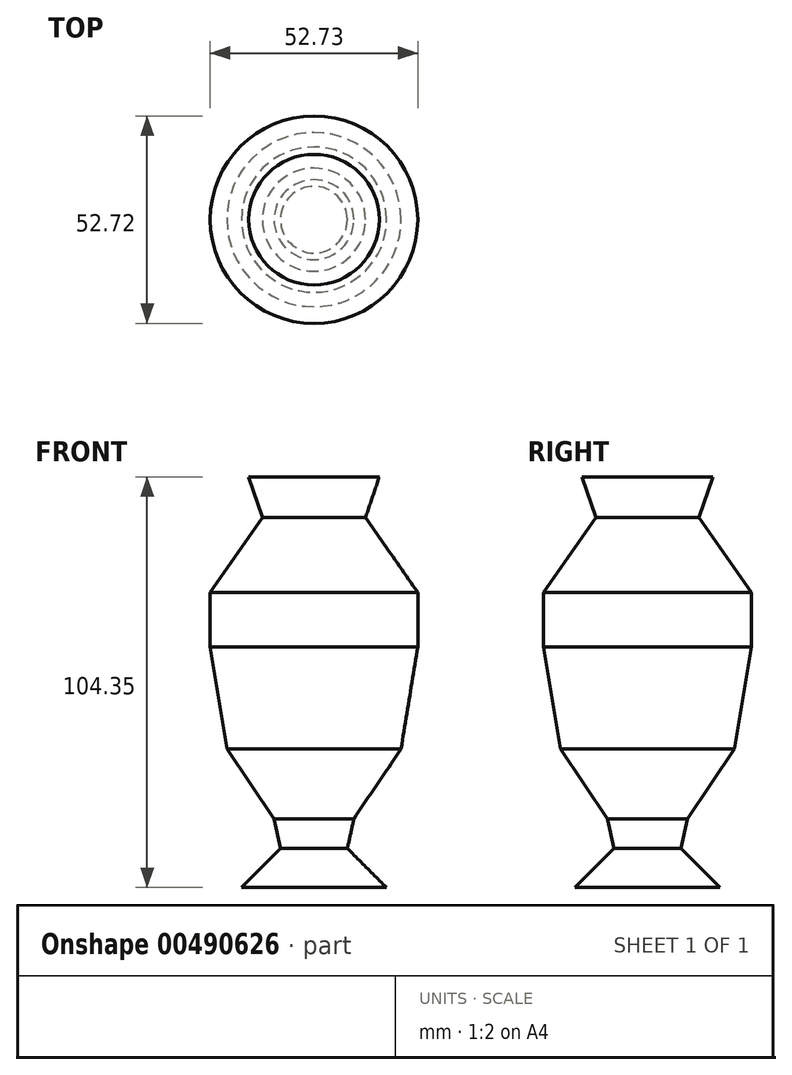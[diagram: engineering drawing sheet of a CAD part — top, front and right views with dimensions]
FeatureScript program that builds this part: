
annotation { "Feature Type Name" : "Feature", "Feature Type Description" : "" }
export const myFeature = defineFeature(function(context is Context, id is Id, definition is map)
    precondition{}
    {
        {
            var Q0;
            Q0=qCreatedBy(makeId("Front.planeOp"),FACE);
            var sketch = newSketch(context, id + "F0", { "sketchPlane" : qUnion([Q0])});
            skLineSegment(sketch, "E0", {"start": v(-34.1, 48.12) * mm, "end": v(-17.51, 48.12) * mm});
            skLineSegment(sketch, "E1", {"start": v(-17.51, 48.12) * mm, "end": v(-17.51, -56.23) * mm});
            skLineSegment(sketch, "E2", {"start": v(-17.51, -56.23) * mm, "end": v(-35.95, -56.23) * mm});
            skLineSegment(sketch, "E3", {"start": v(-35.95, -56.23) * mm, "end": v(-26, -46.27) * mm});
            skLineSegment(sketch, "E4", {"start": v(-26, -46.27) * mm, "end": v(-27.65, -38.71) * mm});
            skLineSegment(sketch, "E5", {"start": v(-27.65, -38.71) * mm, "end": v(-39.64, -21.02) * mm});
            skLineSegment(sketch, "E6", {"start": v(-39.64, -21.02) * mm, "end": v(-43.88, 4.98) * mm});
            skLineSegment(sketch, "E7", {"start": v(-43.88, 4.98) * mm, "end": v(-43.88, 18.8) * mm});
            skLineSegment(sketch, "E8", {"start": v(-43.88, 18.8) * mm, "end": v(-30.6, 37.8) * mm});
            skLineSegment(sketch, "E9", {"start": v(-30.6, 37.8) * mm, "end": v(-34.1, 48.12) * mm});
            skSolve(sketch);
        }
        {
            var Q0;
            Q0=makeQuery(id+"F0.imprint","IMPRINT",FACE,{"disambiguationData":[TD([[makeQuery(id+"F0.imprint","IMPRINT",EDGE,{"derivedFrom":sQuery(id+"F0.wireOp",EDGE,"E0")}),-1.0]])]});
            var Q1;
            Q1=sQuery(id+"F0.wireOp",EDGE,"E1");
            revolve(context, id + "F1", {"entities" : qUnion([Q0]), "axis" : qUnion([Q1]), "revolveType" : RevolveType.FULL});
        }
    });
